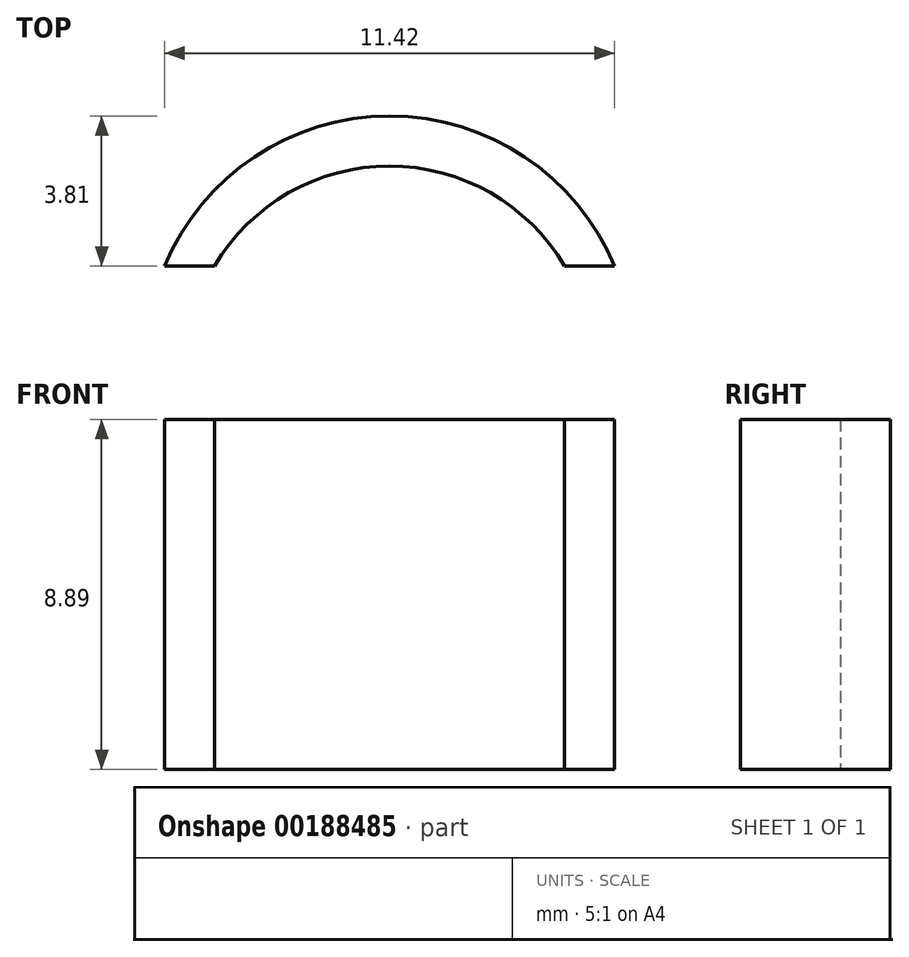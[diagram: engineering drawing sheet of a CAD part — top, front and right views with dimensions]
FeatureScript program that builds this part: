
annotation { "Feature Type Name" : "Feature", "Feature Type Description" : "" }
export const myFeature = defineFeature(function(context is Context, id is Id, definition is map)
    precondition{}
    {
        {
            var Q0;
            Q0=qCreatedBy(makeId("Top.planeOp"),FACE);
            var sketch = newSketch(context, id + "F0", { "sketchPlane" : qUnion([Q0])});
            skLineSegment(sketch, "E0", {"start": v(5.72, 0) * mm, "end": v(4.45, 0) * mm});
            skLineSegment(sketch, "E1", {"start": v(-5.71, 0) * mm, "end": v(-4.45, 0) * mm});
            skLineSegment(sketch, "E2", {"start": v(0, 0) * mm, "end": v(0, 3.81) * mm});
            skLineSegment(sketch, "E3", {"start": v(0, 0) * mm, "end": v(0, 2.54) * mm});
            skArc(sketch, "E4", {"start": v(5.71, 0) * mm, "mid": v(0, 3.8) * mm, "end": v(-5.72, 0) * mm});
            skArc(sketch, "E5", {"start": v(4.45, 0) * mm, "mid": v(0, 2.54) * mm, "end": v(-4.45, 0) * mm});
            skSolve(sketch);
        }
        {
            var Q0;
            Q0 = qSketchRegion(id + "F0", true);
            extrude(context, id + "F1", {"entities" : qUnion([Q0]), "depth" : 8.9 * mm});
        }
    });
